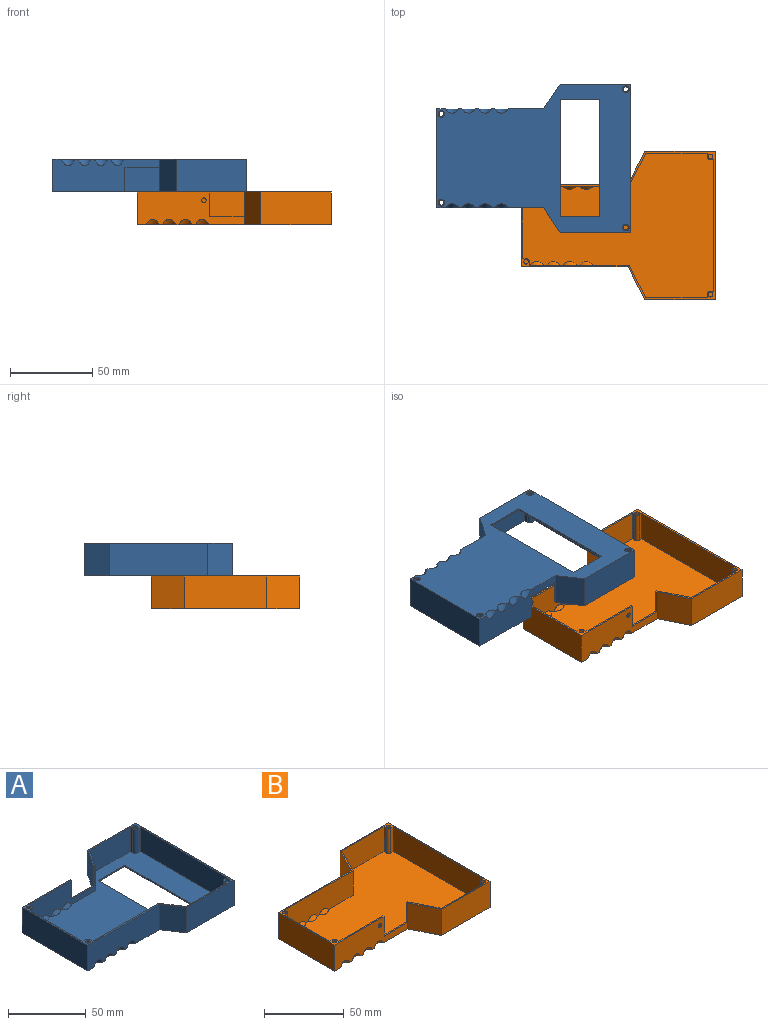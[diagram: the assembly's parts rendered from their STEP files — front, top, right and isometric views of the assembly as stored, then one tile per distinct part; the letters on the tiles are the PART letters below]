
ASSEMBLY  parts=2 mates=1
PART A: 64 faces, bbox 118x90x23 mm
  f0: plane 118x90mm, normal (0,0,1), area 425.4mm2, adj f1,f3,f4,f6,f7,f8,f9,f10
  f1: plane 65x20mm, normal (0,1,0), area 895.9mm2, adj f0,f2,f9,f14,f15,f17,f19,f21
  f2: plane 118x90mm, normal (0,0,-1), area 6652.7mm2, adj f1,f8,f9,f10,f11,f12,f13,f14
  f3: plane 49x19mm, normal (1,0,0), area 931mm2, adj f0,f5,f43,f48
  f4: plane 36.97x19mm, normal (0,1,0), area 702.3mm2, adj f0,f5,f25,f39
  f5: plane 116x88mm, normal (0,0,1), area 6249.3mm2, adj f3,f4,f6,f7,f23,f24,f25,f26
  f6: plane 79x19mm, normal (-1,0,0), area 1501mm2, adj f0,f5,f38,f42
  f7: plane 36.97x19mm, normal (0,-1,0), area 702.3mm2, adj f0,f5,f26,f35
  f8: plane 65x20mm, normal (0,-1,0), area 1210.9mm2, adj f0,f2,f9,f10,f16,f18,f20,f22
  f9: plane 60x20mm, normal (-1,0,0), area 1200mm2, adj f0,f1,f2,f8
  f10: plane 20x15mm, normal (-0.83,-0.55,0), area 360.6mm2, adj f0,f2,f8,f11
  f11: plane 43x20mm, normal (0,-1,0), area 860mm2, adj f0,f2,f10,f12
  f12: plane 90x20mm, normal (1,0,0), area 1800mm2, adj f0,f2,f11,f13
  f13: plane 43x20mm, normal (0,1,0), area 860mm2, adj f0,f2,f12,f14
  f14: plane 20x15mm, normal (-0.83,0.55,0), area 360.6mm2, adj f0,f1,f2,f13,f63
  f15: torus R=39mm, axis (1,0,0), area 28.8mm2, adj f1,f2
  f16: torus R=39mm, axis (1,0,0), area 28.8mm2, adj f2,f8
  f17: torus R=39mm, axis (1,0,0), area 28.8mm2, adj f1,f2
  f18: torus R=39mm, axis (1,0,0), area 28.8mm2, adj f2,f8
  f19: torus R=39mm, axis (1,0,0), area 28.8mm2, adj f1,f2
  f20: torus R=39mm, axis (1,0,0), area 28.8mm2, adj f2,f8
  f21: torus R=39mm, axis (1,0,0), area 28.8mm2, adj f1,f2
  f22: torus R=39mm, axis (1,0,0), area 28.8mm2, adj f2,f8
  f23: plane 60.19x19mm, normal (0,1,0), area 1070.3mm2, adj f0,f5,f25,f28,f30,f32,f34,f52
  f24: plane 60.19x19mm, normal (0,-1,0), area 755.3mm2, adj f0,f5,f26,f27,f29,f31,f33,f47
  f25: plane 19x15mm, normal (0.83,0.55,0), area 342.5mm2, adj f0,f4,f5,f23
  f26: plane 19x15mm, normal (0.83,-0.55,0), area 342.5mm2, adj f0,f5,f7,f24
  f27: torus R=39mm, axis (1,0,0), area 22.9mm2, adj f5,f24
  f28: torus R=39mm, axis (1,0,0), area 22.9mm2, adj f5,f23
  f29: torus R=39mm, axis (1,0,0), area 22.9mm2, adj f5,f24
  f30: torus R=39mm, axis (1,0,0), area 22.9mm2, adj f5,f23
  f31: torus R=39mm, axis (1,0,0), area 22.9mm2, adj f5,f24
  f32: torus R=39mm, axis (1,0,0), area 22.9mm2, adj f5,f23
  f33: torus R=39mm, axis (1,0,0), area 22.9mm2, adj f5,f24,f47
  f34: torus R=39mm, axis (1,0,0), area 22.9mm2, adj f5,f23,f52
  f35: plane 19x2.25mm, normal (-1,0,0), area 42.7mm2, adj f0,f5,f7,f36
  f36: cylinder r=2.25mm len=19mm, axis (0,0,-1), area 67.2mm2, adj f0,f5,f35,f38
  f37: cylinder r=1.5mm len=19.5mm, axis (0,0,-1), area 183.8mm2, adj f0,f58
  f38: plane 19x2.25mm, normal (0,-1,0), area 42.8mm2, adj f0,f5,f6,f36
  f39: plane 19x2.25mm, normal (-1,0,0), area 42.7mm2, adj f0,f4,f5,f40
  f40: cylinder r=2.25mm len=19mm, axis (0,0,-1), area 67.2mm2, adj f0,f5,f39,f42
  f41: cylinder r=1.5mm len=19.5mm, axis (0,0,-1), area 183.8mm2, adj f0,f57
  f42: plane 19x2.25mm, normal (0,1,0), area 42.8mm2, adj f0,f5,f6,f40
  f43: plane 19x2.25mm, normal (0,-1,0), area 42.7mm2, adj f0,f3,f5,f44
  f44: cylinder r=2.25mm len=19mm, axis (0,0,-1), area 67.2mm2, adj f0,f5,f43,f45
  f45: plane 19x2.08mm, normal (1,0,0), area 39.5mm2, adj f0,f5,f44,f47
  f46: cylinder r=1.5mm len=19.5mm, axis (0,0,-1), area 183.8mm2, adj f0,f60
  f47: extruded ~19x0.17mm, area 4.3mm2, adj f0,f24,f33,f45
  f48: plane 19x2.25mm, normal (0,1,0), area 42.7mm2, adj f0,f3,f5,f49
  f49: cylinder r=2.25mm len=19mm, axis (0,0,-1), area 67.2mm2, adj f0,f5,f48,f50
  f50: plane 19x2.08mm, normal (1,0,0), area 39.5mm2, adj f0,f5,f49,f52
  f51: cylinder r=1.5mm len=19.5mm, axis (0,0,-1), area 183.8mm2, adj f0,f59
  f52: extruded ~19x0.17mm, area 4.3mm2, adj f0,f23,f34,f50
  f53: plane 71x1mm, normal (1,0,0), area 71mm2, adj f2,f5,f54,f56
  f54: plane 24x1mm, normal (0,1,0), area 24mm2, adj f2,f5,f53,f55
  f55: plane 71x1mm, normal (-1,0,0), area 71mm2, adj f2,f5,f54,f56
  f56: plane 24x1mm, normal (0,-1,0), area 24mm2, adj f2,f5,f53,f55
  f57: cone r=1.5mm half-angle=45deg, axis (0,0,-1), area 7.8mm2, adj f2,f41
  f58: cone r=2mm half-angle=45deg, axis (0,0,-1), area 7.8mm2, adj f2,f37
  f59: cone r=1.5mm half-angle=45deg, axis (0,0,-1), area 7.8mm2, adj f2,f51
  f60: cone r=2mm half-angle=45deg, axis (0,0,-1), area 7.8mm2, adj f2,f46
  f61: plane 15x1mm, normal (1,0,0), area 15mm2, adj f0,f1,f24,f62
  f62: plane 21x1mm, normal (0,0,1), area 21mm2, adj f1,f24,f61,f63
  f63: plane 15x1mm, normal (-1,0,0), area 15mm2, adj f0,f14,f24,f62
PART B: 59 faces, bbox 118x90x23.4 mm
  f0: plane 116x88mm, normal (0,0,1), area 7269mm2, adj f1,f2,f3,f4,f6,f24,f25,f26
  f1: plane 40x19mm, normal (1,0,0), area 760mm2, adj f0,f5,f48,f53
  f2: plane 37.38x19mm, normal (0,1,0), area 710.3mm2, adj f0,f5,f25,f43
  f3: plane 80x19mm, normal (-1,0,0), area 1520mm2, adj f0,f5,f41,f46
  f4: plane 37.38x19mm, normal (0,-1,0), area 710.3mm2, adj f0,f5,f26,f38
  f5: plane 118x90mm, normal (0,0,1), area 411.7mm2, adj f1,f2,f3,f4,f6,f7,f8,f10
  f6: plane 60.62x19mm, normal (0,1,0), area 770mm2, adj f0,f5,f25,f28,f30,f32,f34,f35
  f7: plane 65x20mm, normal (0,-1,0), area 903mm2, adj f5,f9,f10,f11,f17,f19,f21,f23
  f8: plane 65x20mm, normal (0,1,0), area 1224.2mm2, adj f5,f9,f10,f15,f16,f18,f20,f22
  f9: plane 118x90mm, normal (0,0,-1), area 7702.1mm2, adj f7,f8,f10,f11,f12,f13,f14,f15
  f10: plane 50x20mm, normal (-1,0,0), area 1000mm2, adj f5,f7,f8,f9
  f11: plane 20x20mm, normal (-0.89,-0.45,0), area 447.2mm2, adj f5,f7,f9,f12,f36
  f12: plane 43x20mm, normal (0,-1,0), area 860mm2, adj f5,f9,f11,f13
  f13: plane 90x20mm, normal (1,0,0), area 1800mm2, adj f5,f9,f12,f14
  f14: plane 43x20mm, normal (0,1,0), area 860mm2, adj f5,f9,f13,f15
  f15: plane 20x20mm, normal (-0.89,0.45,0), area 447.2mm2, adj f5,f8,f9,f14
  f16: torus R=35mm, axis (1,0,0), area 26.2mm2, adj f8,f9
  f17: torus R=35mm, axis (1,0,0), area 26.2mm2, adj f7,f9
  f18: torus R=35mm, axis (1,0,0), area 26.2mm2, adj f8,f9
  f19: torus R=35mm, axis (1,0,0), area 26.2mm2, adj f7,f9
  f20: torus R=35mm, axis (1,0,0), area 26.2mm2, adj f8,f9
  f21: torus R=35mm, axis (1,0,0), area 26.2mm2, adj f7,f9
  f22: torus R=35mm, axis (1,0,0), area 26.2mm2, adj f8,f9
  f23: torus R=35mm, axis (1,0,0), area 26.2mm2, adj f7,f9
  f24: plane 60.62x19mm, normal (0,-1,0), area 1091.2mm2, adj f0,f5,f26,f27,f29,f31,f33,f51
  f25: plane 20x19mm, normal (0.89,0.45,0), area 424.9mm2, adj f0,f2,f5,f6
  f26: plane 20x19mm, normal (0.89,-0.45,0), area 424.9mm2, adj f0,f4,f5,f24
  f27: torus R=35mm, axis (1,0,0), area 20.2mm2, adj f0,f24
  f28: torus R=35mm, axis (1,0,0), area 20.2mm2, adj f0,f6
  f29: torus R=35mm, axis (1,0,0), area 20.2mm2, adj f0,f24
  f30: torus R=35mm, axis (1,0,0), area 20.2mm2, adj f0,f6
  f31: torus R=35mm, axis (1,0,0), area 20.2mm2, adj f0,f24
  f32: torus R=35mm, axis (1,0,0), area 20.2mm2, adj f0,f6
  f33: torus R=35mm, axis (1,0,0), area 20.2mm2, adj f0,f24
  f34: torus R=35mm, axis (1,0,0), area 20.2mm2, adj f0,f6
  f35: plane 21x1mm, normal (0,0,1), area 21mm2, adj f6,f7,f36,f37
  f36: plane 15x1mm, normal (-1,0,0), area 15mm2, adj f5,f6,f11,f35
  f37: plane 15x1mm, normal (1,0,0), area 15mm2, adj f5,f6,f7,f35
  f38: plane 19x2mm, normal (-1,0,0), area 38mm2, adj f0,f4,f5,f39
  f39: cylinder r=2mm len=19mm, axis (0,0,-1), area 59.7mm2, adj f0,f5,f38,f41
  f40: cylinder r=1.4mm len=19mm, axis (0,0,-1), area 167.1mm2, adj f5,f42
  f41: plane 19x2mm, normal (0,-1,0), area 38mm2, adj f0,f3,f5,f39
  f42: plane 2.8x2.8mm, normal (0,0,1), area 6.2mm2, adj f40
  f43: plane 19x2mm, normal (-1,0,0), area 38mm2, adj f0,f2,f5,f44
  f44: cylinder r=2mm len=19mm, axis (0,0,-1), area 59.7mm2, adj f0,f5,f43,f46
  f45: cylinder r=1.4mm len=19mm, axis (0,0,-1), area 167.1mm2, adj f5,f47
  f46: plane 19x2mm, normal (0,1,0), area 38mm2, adj f0,f3,f5,f44
  f47: plane 2.8x2.8mm, normal (0,0,1), area 6.2mm2, adj f45
  f48: plane 19x2mm, normal (0,-1,0), area 38mm2, adj f0,f1,f5,f49
  f49: cylinder r=2mm len=19mm, axis (0,0,-1), area 59.7mm2, adj f0,f5,f48,f51
  f50: cylinder r=1.4mm len=19mm, axis (0,0,-1), area 167.1mm2, adj f5,f52
  f51: plane 19x2mm, normal (1,0,0), area 38mm2, adj f0,f5,f24,f49
  f52: plane 2.8x2.8mm, normal (0,0,1), area 6.2mm2, adj f50
  f53: plane 19x2mm, normal (0,1,0), area 38mm2, adj f0,f1,f5,f54
  f54: cylinder r=2mm len=19mm, axis (0,0,-1), area 59.7mm2, adj f0,f5,f53,f56
  f55: cylinder r=1.4mm len=19mm, axis (0,0,-1), area 167.1mm2, adj f5,f57
  f56: plane 19x2mm, normal (1,0,0), area 38mm2, adj f0,f5,f6,f54
  f57: plane 2.8x2.8mm, normal (0,0,1), area 6.2mm2, adj f55
  f58: cylinder r=1.4mm len=2.8mm, axis (0,-1,0), area 8.8mm2, adj f6,f7
PLACE A rot(axis=(1,0,0),180deg) t=(-51.41,65.75,40)mm
PLACE B t=(0,25,0)mm
MATE revolute A.f0 <-> B.f5  axis (0,0,-1) through (65.59,26.25,20)mm
